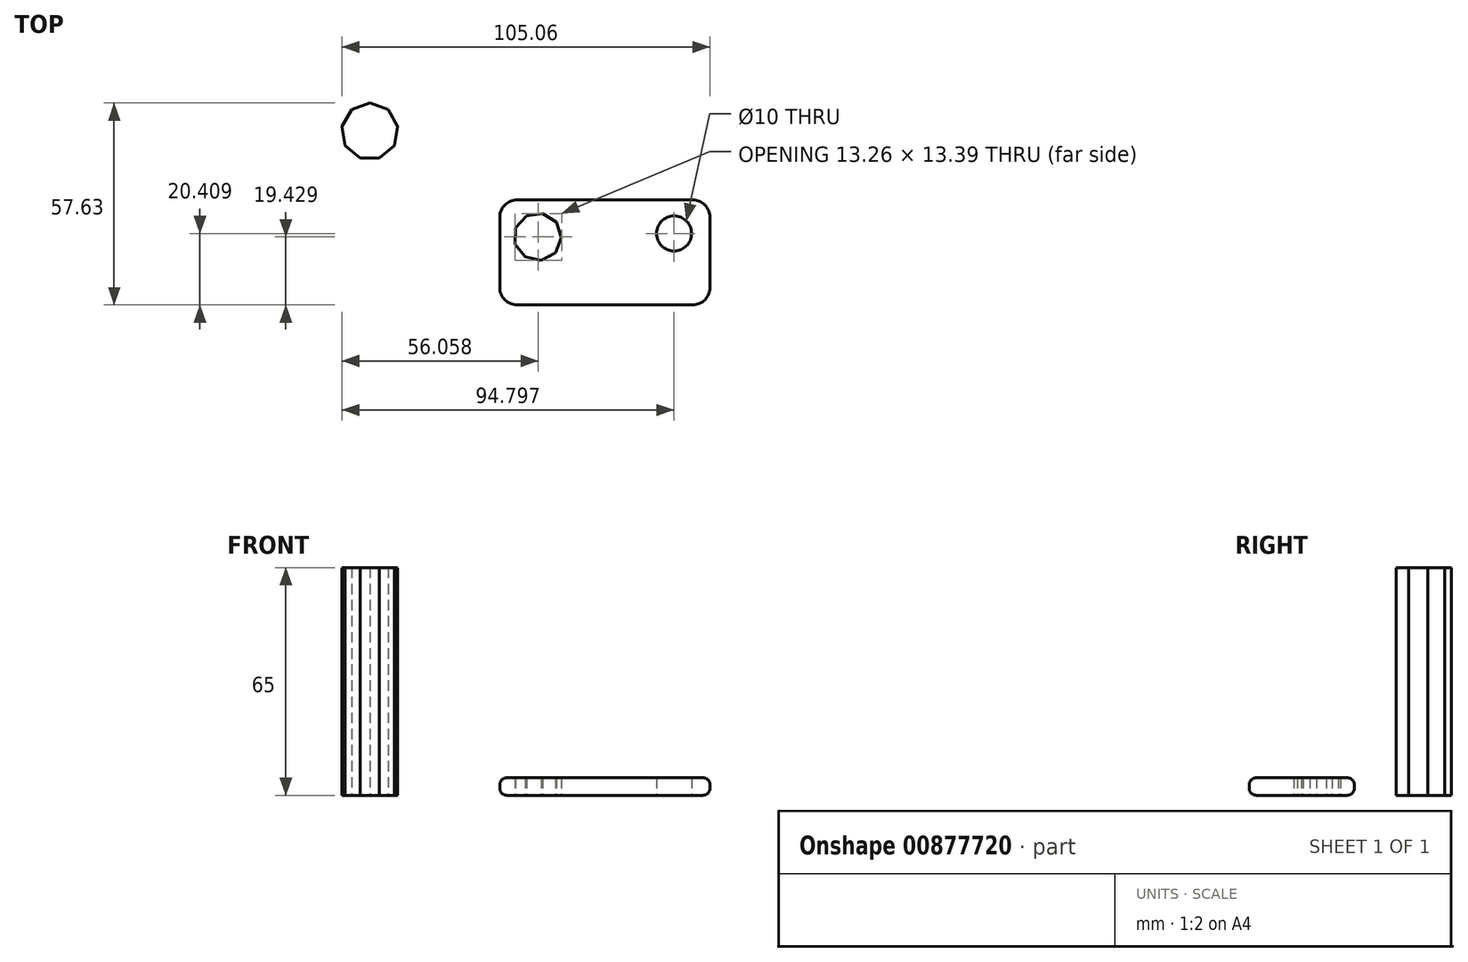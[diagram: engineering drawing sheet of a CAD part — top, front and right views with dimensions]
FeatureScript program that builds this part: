
annotation { "Feature Type Name" : "Feature", "Feature Type Description" : "" }
export const myFeature = defineFeature(function(context is Context, id is Id, definition is map)
    precondition{}
    {
        {
            var Q0;
            Q0=qCreatedBy(makeId("Top.planeOp"),FACE);
            var sketch = newSketch(context, id + "F0", { "sketchPlane" : qUnion([Q0])});
            skLineSegment(sketch, "E0.bottom", {"start": v(-25.2, 13.82) * mm, "end": v(34.8, 13.82) * mm});
            skLineSegment(sketch, "E0.top", {"start": v(-25.2, -16.18) * mm, "end": v(34.8, -16.18) * mm});
            skLineSegment(sketch, "E0.left", {"start": v(-25.2, 13.82) * mm, "end": v(-25.2, -16.18) * mm});
            skLineSegment(sketch, "E0.right", {"start": v(34.8, 13.82) * mm, "end": v(34.8, -16.18) * mm});
            skSolve(sketch);
        }
        {
            var Q0;
            Q0=makeQuery(id+"F0.imprint","IMPRINT",FACE,{"disambiguationData":[TD([[makeQuery(id+"F0.imprint","IMPRINT",EDGE,{"derivedFrom":sQuery(id+"F0.wireOp",EDGE,"E0.bottom")}),-1.0]])]});
            extrude(context, id + "F1", {"entities" : qUnion([Q0]), "depth" : 5 * mm, "offsetDistance" : 25 * mm});
        }
        {
            var Q0;
            Q0=makeQuery(id+"F1.opExtrude","SWEPT_EDGE",EDGE,{"disambiguationData":[OSD([sQuery(id+"F0.wireOp",EDGE,"E0.top"),sQuery(id+"F0.wireOp",EDGE,"E0.left")])]});
            var Q1;
            Q1=makeQuery(id+"F1.opExtrude","SWEPT_EDGE",EDGE,{"disambiguationData":[OSD([sQuery(id+"F0.wireOp",EDGE,"E0.top"),sQuery(id+"F0.wireOp",EDGE,"E0.right")])]});
            var Q2;
            Q2=makeQuery(id+"F1.opExtrude","SWEPT_EDGE",EDGE,{"disambiguationData":[OSD([sQuery(id+"F0.wireOp",EDGE,"E0.bottom"),sQuery(id+"F0.wireOp",EDGE,"E0.right")])]});
            var Q3;
            Q3=makeQuery(id+"F1.opExtrude","SWEPT_EDGE",EDGE,{"disambiguationData":[OSD([sQuery(id+"F0.wireOp",EDGE,"E0.bottom"),sQuery(id+"F0.wireOp",EDGE,"E0.left")])]});
            fillet(context, id + "F2", {"entities" : qUnion([Q0, Q1, Q2, Q3]), "radius" : 5 * mm, "tangentPropagation" : true, "allowEdgeOverflow" : false});
        }
        {
            var Q0;
            Q0=makeQuery(id+"F1.opExtrude","CAP_EDGE",EDGE,{"disambiguationData":[OSD([sQuery(id+"F0.wireOp",EDGE,"E0.top")])],"isStart":false});
            var Q1;
            Q1=makeQuery(id+"F1.opExtrude","CAP_EDGE",EDGE,{"disambiguationData":[OSD([sQuery(id+"F0.wireOp",EDGE,"E0.left")])],"isStart":false});
            var Q2;
            Q2=makeQuery(id+"F1.opExtrude","CAP_EDGE",EDGE,{"disambiguationData":[OSD([sQuery(id+"F0.wireOp",EDGE,"E0.bottom")])],"isStart":false});
            var Q3;
            Q3=makeQuery(id+"F1.opExtrude","CAP_EDGE",EDGE,{"disambiguationData":[OSD([sQuery(id+"F0.wireOp",EDGE,"E0.right")])],"isStart":false});
            fillet(context, id + "F3", {"entities" : qUnion([Q0, Q1, Q2, Q3]), "radius" : 2 * mm, "tangentPropagation" : true, "allowEdgeOverflow" : false});
        }
        {
            var Q0;
            Q0=makeQuery(id+"F1.opExtrude","CAP_EDGE",EDGE,{"disambiguationData":[OSD([sQuery(id+"F0.wireOp",EDGE,"E0.top")])],"isStart":true});
            var Q1;
            Q1=makeQuery(id+"F1.opExtrude","CAP_EDGE",EDGE,{"disambiguationData":[OSD([sQuery(id+"F0.wireOp",EDGE,"E0.left")])],"isStart":true});
            var Q2;
            Q2=makeQuery(id+"F1.opExtrude","CAP_EDGE",EDGE,{"disambiguationData":[OSD([sQuery(id+"F0.wireOp",EDGE,"E0.bottom")])],"isStart":true});
            var Q3;
            Q3=makeQuery(id+"F1.opExtrude","CAP_EDGE",EDGE,{"disambiguationData":[OSD([sQuery(id+"F0.wireOp",EDGE,"E0.right")])],"isStart":true});
            fillet(context, id + "F4", {"entities" : qUnion([Q0, Q1, Q2, Q3]), "radius" : 2 * mm, "tangentPropagation" : true, "allowEdgeOverflow" : false});
        }
        {
            var Q0;
            Q0=makeQuery(id+"F1.opExtrude","CAP_FACE",FACE,{"disambiguationData":[OSD([sQuery(id+"F0.wireOp",EDGE,"E0.bottom"),sQuery(id+"F0.wireOp",EDGE,"E0.top"),sQuery(id+"F0.wireOp",EDGE,"E0.left"),sQuery(id+"F0.wireOp",EDGE,"E0.right")])],"isStart":false});
            var sketch = newSketch(context, id + "F5", { "sketchPlane" : qUnion([Q0])});
            skCircle(sketch, "E1", {"center": v(24.53, 4.23) * mm, "radius": 5 * mm});
            skSolve(sketch);
        }
        {
            var Q0;
            Q0=makeQuery(id+"F5.imprint","IMPRINT",FACE,{"disambiguationData":[TD([[makeQuery(id+"F5.imprint","IMPRINT",EDGE,{"derivedFrom":sQuery(id+"F5.wireOp",EDGE,"E1")}),1.0]])]});
            extrude(context, id + "F6", {"entities" : qUnion([Q0]), "operationType" : NewBodyOperationType.REMOVE, "endBound" : BoundingType.SYMMETRIC, "depth" : -25 * mm, "offsetDistance" : 25 * mm});
        }
        {
            var Q0;
            Q0=makeQuery(id+"F1.opExtrude","CAP_FACE",FACE,{"disambiguationData":[OSD([sQuery(id+"F0.wireOp",EDGE,"E0.bottom"),sQuery(id+"F0.wireOp",EDGE,"E0.top"),sQuery(id+"F0.wireOp",EDGE,"E0.left"),sQuery(id+"F0.wireOp",EDGE,"E0.right")])],"isStart":false});
            var sketch = newSketch(context, id + "F7", { "sketchPlane" : qUnion([Q0])});
            skCircle(sketch, "E2.cCircle", {"center": v(-14.38, 3.29) * mm, "radius": 6.4 * mm, "construction": true});
            skLineSegment(sketch, "E2.0", {"start": v(-9.32, -1.25) * mm, "end": v(-13.42, -3.44) * mm});
            skLineSegment(sketch, "E2.1", {"start": v(-13.42, -3.44) * mm, "end": v(-17.97, -2.48) * mm});
            skLineSegment(sketch, "E2.2", {"start": v(-17.97, -2.48) * mm, "end": v(-20.84, 1.18) * mm});
            skLineSegment(sketch, "E2.3", {"start": v(-20.84, 1.18) * mm, "end": v(-20.69, 5.83) * mm});
            skLineSegment(sketch, "E2.4", {"start": v(-20.69, 5.83) * mm, "end": v(-17.58, 9.29) * mm});
            skLineSegment(sketch, "E2.5", {"start": v(-17.58, 9.29) * mm, "end": v(-12.97, 9.94) * mm});
            skLineSegment(sketch, "E2.6", {"start": v(-12.97, 9.94) * mm, "end": v(-9.02, 7.48) * mm});
            skLineSegment(sketch, "E2.7", {"start": v(-9.02, 7.48) * mm, "end": v(-7.58, 3.06) * mm});
            skLineSegment(sketch, "E2.8", {"start": v(-7.58, 3.06) * mm, "end": v(-9.32, -1.25) * mm});
            skPoint(sketch, "E2.0.midPoint", {"position": v(-11.37, -2.35) * mm});
            skSolve(sketch);
        }
        {
            var Q0;
            Q0=makeQuery(id+"F7.imprint","IMPRINT",FACE,{"disambiguationData":[TD([[makeQuery(id+"F7.imprint","IMPRINT",EDGE,{"derivedFrom":sQuery(id+"F7.wireOp",EDGE,"E2.0")}),-1.0]])]});
            extrude(context, id + "F8", {"entities" : qUnion([Q0]), "operationType" : NewBodyOperationType.REMOVE, "endBound" : BoundingType.SYMMETRIC, "depth" : -25 * mm, "offsetDistance" : 25 * mm});
        }
        {
            var Q0;
            Q0=qCreatedBy(makeId("Top.planeOp"),FACE);
            var sketch = newSketch(context, id + "F9", { "sketchPlane" : qUnion([Q0])});
            skCircle(sketch, "E3.cCircle", {"center": v(-62.3, 33.36) * mm, "radius": 7.6 * mm, "construction": true});
            skLineSegment(sketch, "E3.0", {"start": v(-55.3, 29.31) * mm, "end": v(-59.54, 25.76) * mm});
            skLineSegment(sketch, "E3.1", {"start": v(-59.54, 25.76) * mm, "end": v(-65.07, 25.76) * mm});
            skLineSegment(sketch, "E3.2", {"start": v(-65.07, 25.76) * mm, "end": v(-69.31, 29.32) * mm});
            skLineSegment(sketch, "E3.3", {"start": v(-69.31, 29.32) * mm, "end": v(-70.27, 34.77) * mm});
            skLineSegment(sketch, "E3.4", {"start": v(-70.27, 34.77) * mm, "end": v(-67.5, 39.56) * mm});
            skLineSegment(sketch, "E3.5", {"start": v(-67.5, 39.56) * mm, "end": v(-62.3, 41.45) * mm});
            skLineSegment(sketch, "E3.6", {"start": v(-62.3, 41.45) * mm, "end": v(-57.1, 39.56) * mm});
            skLineSegment(sketch, "E3.7", {"start": v(-57.1, 39.56) * mm, "end": v(-54.33, 34.76) * mm});
            skLineSegment(sketch, "E3.8", {"start": v(-54.33, 34.76) * mm, "end": v(-55.3, 29.31) * mm});
            skPoint(sketch, "E3.0.midPoint", {"position": v(-57.42, 27.53) * mm});
            skSolve(sketch);
        }
        {
            var Q0;
            Q0=makeQuery(id+"F9.imprint","IMPRINT",FACE,{"disambiguationData":[TD([[makeQuery(id+"F9.imprint","IMPRINT",EDGE,{"derivedFrom":sQuery(id+"F9.wireOp",EDGE,"E3.0")}),-1.0]])]});
            extrude(context, id + "F10", {"entities" : qUnion([Q0]), "depth" : 65 * mm, "offsetDistance" : 25 * mm});
        }
    });
